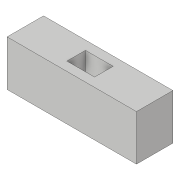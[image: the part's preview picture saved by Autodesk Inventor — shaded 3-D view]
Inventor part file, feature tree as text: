
AUTODESK INVENTOR PART (.ipt)
format: ipt  version: 2018.3 (Build 223284000, 284)  size: 105,984 bytes
history: native  units: in
note: dims shown in document units (in); Inventor stores cm internally (conversion verified against a paired STEP export)
features: extrude x3, sketch x3
ambient origin geometry x8: Origin, YZ Plane, XZ Plane, XY Plane, X Axis, Y Axis, Z Axis, Center Point
bodies: Solid1 (feature_tree)
feature tree (6):
  extrude  "Extrusion1"  Depth=1.25in
  extrude  "Extrusion2"  Depth=1.0in
  extrude  "Extrusion3"  Depth=0.245in
  sketch  "Sketch1"  dims[d0=3.55in d1=1.25in]
  sketch  "Sketch2"  dims[d2=1.0in d3=0.0in d4=1.5in]
  sketch  "Sketch3"  dims[d5=1.5in d6=0.245in d7=0.245in d8=0.255in d10=0.275in d11=0.275in d12=0.51in d13=3.0in d14=0.0in d15=0.125in d16=0.125in d17=0.0in d18=0.0in d19=0.125in d20=0.125in d21=3.0in d22=0.0in]
